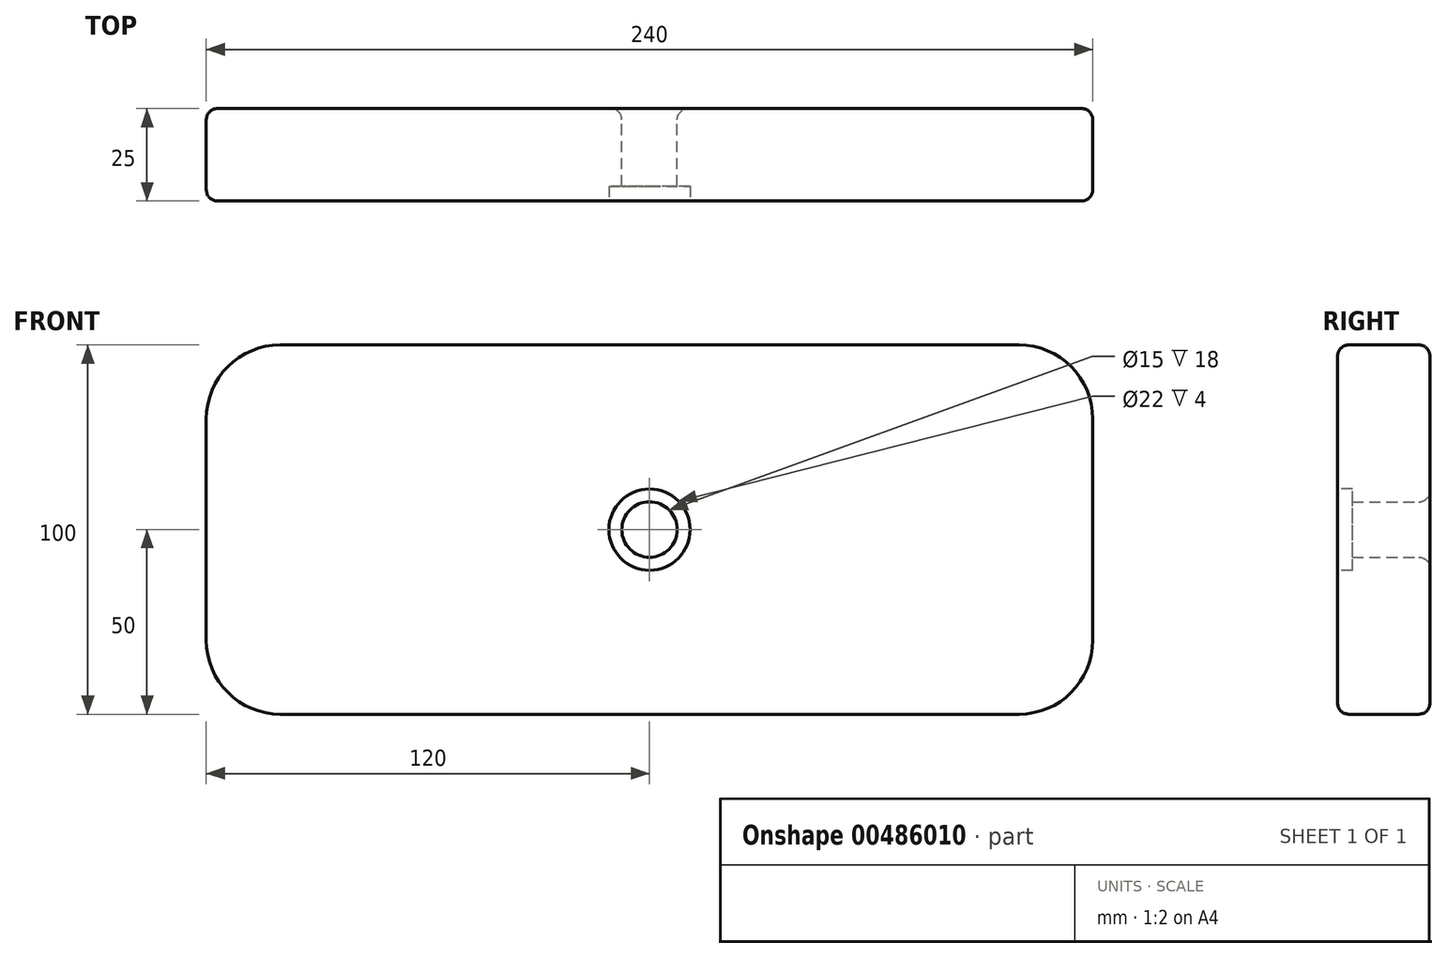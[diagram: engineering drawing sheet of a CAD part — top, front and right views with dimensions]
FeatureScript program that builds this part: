
annotation { "Feature Type Name" : "Feature", "Feature Type Description" : "" }
export const myFeature = defineFeature(function(context is Context, id is Id, definition is map)
    precondition{}
    {
        {
            var Q0;
            Q0=qCreatedBy(makeId("Front.planeOp"),FACE);
            var sketch = newSketch(context, id + "F0", { "sketchPlane" : qUnion([Q0])});
            skLineSegment(sketch, "E0.bottom", {"start": v(-100, 50) * mm, "end": v(100, 50) * mm});
            skLineSegment(sketch, "E0.top", {"start": v(-100, -50) * mm, "end": v(100, -50) * mm});
            skLineSegment(sketch, "E0.left", {"start": v(-120, 30) * mm, "end": v(-120, -30) * mm});
            skLineSegment(sketch, "E0.right", {"start": v(120, 30) * mm, "end": v(120, -30) * mm});
            skPoint(sketch, "E0.middle", {"position": v(0, 0) * mm});
            skPoint(sketch, "E1.visualSharp", {"position": v(-120, 50) * mm});
            skArc(sketch, "E1.filletArc", {"start": v(-100, 50) * mm, "mid": v(-114.14, 44.14) * mm, "end": v(-120, 30) * mm});
            skPoint(sketch, "E2.visualSharp", {"position": v(120, 50) * mm});
            skArc(sketch, "E2.filletArc", {"start": v(120, 30) * mm, "mid": v(114.14, 44.14) * mm, "end": v(100, 50) * mm});
            skPoint(sketch, "E3.visualSharp", {"position": v(120, -50) * mm});
            skArc(sketch, "E3.filletArc", {"start": v(100, -50) * mm, "mid": v(114.14, -44.14) * mm, "end": v(120, -30) * mm});
            skPoint(sketch, "E4.visualSharp", {"position": v(-120, -50) * mm});
            skArc(sketch, "E4.filletArc", {"start": v(-120, -30) * mm, "mid": v(-114.14, -44.14) * mm, "end": v(-100, -50) * mm});
            skCircle(sketch, "E5", {"center": v(0, 0) * mm, "radius": 7.5 * mm});
            skSolve(sketch);
        }
        {
            var Q0;
            Q0 = qSketchRegion(id + "F0", true);
            extrude(context, id + "F1", {"entities" : qUnion([Q0]), "depth" : 25 * mm});
        }
        {
            var Q0;
            Q0=makeQuery(id+"F1.opExtrude","CAP_EDGE",EDGE,{"disambiguationData":[OSD([sQuery(id+"F0.wireOp",EDGE,"E0.bottom")])],"isStart":false});
            var Q1;
            Q1=makeQuery(id+"F1.opExtrude","CAP_FACE",FACE,{"disambiguationData":[OSD([sQuery(id+"F0.wireOp",EDGE,"E0.bottom"),sQuery(id+"F0.wireOp",EDGE,"E0.top"),sQuery(id+"F0.wireOp",EDGE,"E0.left"),sQuery(id+"F0.wireOp",EDGE,"E0.right"),sQuery(id+"F0.wireOp",EDGE,"E1.filletArc"),sQuery(id+"F0.wireOp",EDGE,"E2.filletArc"),sQuery(id+"F0.wireOp",EDGE,"E3.filletArc"),sQuery(id+"F0.wireOp",EDGE,"E4.filletArc"),sQuery(id+"F0.wireOp",EDGE,"E5")])],"isStart":true});
            fillet(context, id + "F2", {"entities" : qUnion([Q0, Q1]), "radius" : 3 * mm, "tangentPropagation" : true, "allowEdgeOverflow" : false});
        }
        {
            var Q0;
            Q0=makeQuery(id+"F1.opExtrude","CAP_FACE",FACE,{"disambiguationData":[OSD([sQuery(id+"F0.wireOp",EDGE,"E0.bottom"),sQuery(id+"F0.wireOp",EDGE,"E0.top"),sQuery(id+"F0.wireOp",EDGE,"E0.left"),sQuery(id+"F0.wireOp",EDGE,"E0.right"),sQuery(id+"F0.wireOp",EDGE,"E1.filletArc"),sQuery(id+"F0.wireOp",EDGE,"E2.filletArc"),sQuery(id+"F0.wireOp",EDGE,"E3.filletArc"),sQuery(id+"F0.wireOp",EDGE,"E4.filletArc"),sQuery(id+"F0.wireOp",EDGE,"E5")])],"isStart":false});
            var sketch = newSketch(context, id + "F3", { "sketchPlane" : qUnion([Q0])});
            skCircle(sketch, "E6", {"center": v(0, 0) * mm, "radius": 11 * mm});
            skSolve(sketch);
        }
        {
            var Q0;
            Q0 = qSketchRegion(id + "F3", true);
            extrude(context, id + "F4", {"entities" : qUnion([Q0]), "operationType" : NewBodyOperationType.REMOVE, "oppositeDirection" : true, "depth" : 4 * mm});
        }
    });
